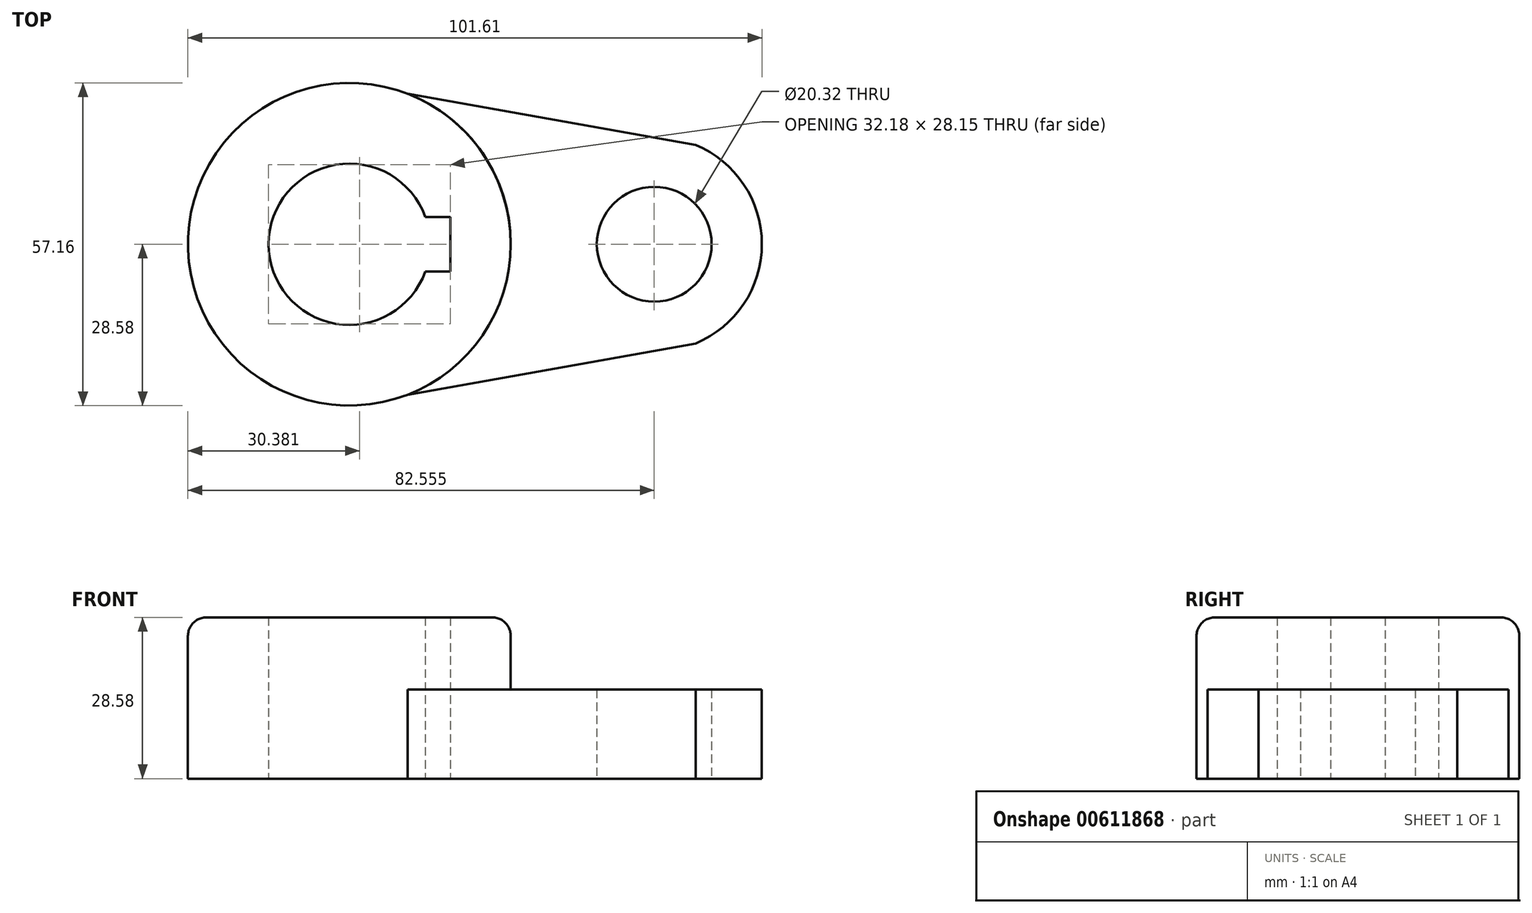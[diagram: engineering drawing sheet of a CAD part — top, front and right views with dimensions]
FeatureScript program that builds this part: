
annotation { "Feature Type Name" : "Feature", "Feature Type Description" : "" }
export const myFeature = defineFeature(function(context is Context, id is Id, definition is map)
    precondition{}
    {
        {
            var Q0;
            Q0=qCreatedBy(makeId("Top.planeOp"),FACE);
            var sketch = newSketch(context, id + "F0", { "sketchPlane" : qUnion([Q0])});
            skArc(sketch, "E0", {"start": v(13.45, 4.83) * mm, "mid": v(-14.29, 0) * mm, "end": v(13.45, -4.83) * mm});
            skCircle(sketch, "E1", {"center": v(0, 0) * mm, "radius": 28.57 * mm});
            skCircle(sketch, "E2", {"center": v(53.98, 0) * mm, "radius": 10.16 * mm});
            skPoint(sketch, "E3.end.orphan", {"position": v(55.86, 16.6) * mm});
            skPoint(sketch, "E4.end.orphan", {"position": v(55.86, -16.71) * mm});
            skArc(sketch, "E5", {"start": v(61.3, 17.58) * mm, "mid": v(73.02, -0.52) * mm, "end": v(60.33, -17.96) * mm});
            skLineSegment(sketch, "E6", {"start": v(10.31, 26.65) * mm, "end": v(61.3, 17.58) * mm});
            skLineSegment(sketch, "E7.MirrorCS", {"start": v(10.31, -26.65) * mm, "end": v(61.3, -17.58) * mm});
            skLineSegment(sketch, "E8.bottom", {"start": v(17.89, 4.83) * mm, "end": v(13.45, 4.83) * mm});
            skLineSegment(sketch, "E8.top", {"start": v(17.89, -4.83) * mm, "end": v(13.45, -4.83) * mm});
            skLineSegment(sketch, "E8.left", {"start": v(17.89, 4.83) * mm, "end": v(17.89, -4.83) * mm});
            skPoint(sketch, "E8.middle", {"position": v(14.29, 0) * mm});
            skLineSegment(sketch, "E9", {"start": v(14.29, 4.83) * mm, "end": v(17.89, 4.83) * mm});
            skPoint(sketch, "E10.endSnap0", {"position": v(14.29, -4.83) * mm});
            skPoint(sketch, "E8.right.start.orphan", {"position": v(10.69, 4.83) * mm});
            skPoint(sketch, "E11.orphan", {"position": v(10.69, -4.83) * mm});
            skSolve(sketch);
        }
        {
            var Q0;
            Q0=makeQuery(id+"F0.imprint","IMPRINT",FACE,{"disambiguationData":[TD([[makeQuery(id+"F0.imprint","IMPRINT",EDGE,{"derivedFrom":sQuery(id+"F0.wireOp",EDGE,"E0")}),-1.0]])]});
            extrude(context, id + "F1", {"entities" : qUnion([Q0]), "depth" : 28.57 * mm, "offsetDistance" : 25.4 * mm});
        }
        {
            var Q0;
            Q0=makeQuery(id+"F0.imprint","IMPRINT",FACE,{"disambiguationData":[TD([[makeQuery(id+"F0.imprint","IMPRINT",EDGE,{"derivedFrom":sQuery(id+"F0.wireOp",EDGE,"E2")}),-1.0]])]});
            extrude(context, id + "F2", {"entities" : qUnion([Q0]), "operationType" : NewBodyOperationType.ADD, "depth" : 15.77 * mm, "offsetDistance" : 25.4 * mm});
        }
        {
            var Q0;
            Q0=makeQuery(id+"F1.opExtrude","CAP_EDGE",EDGE,{"disambiguationData":[OSD([sQuery(id+"F0.wireOp",EDGE,"E1")])],"isStart":false});
            fillet(context, id + "F3", {"entities" : qUnion([Q0]), "radius" : 3.3 * mm, "tangentPropagation" : true, "allowEdgeOverflow" : false});
        }
    });
